# Revit family: FS_Reynaers_SL38 Cubic_Window Fixed
name_source: partatom
category: Окна
revit_build: Autodesk Revit 2017 (Build: 20160225_1515(x64)
units: mm (PartAtom-declared; Revit-internal decimal feet)

## family parameters
Всегда вертикально = Да
Заголовок OmniClass = Windows
Номер OmniClass = 23.30.20.00
Общий = Нет
Основа = Стена
При загрузке вырезать с полостями = Нет
Точка расчета площади = Нет

## types (1)
- Frame 38.5
    BE = Да
    Date of publishing = 2015-11-19
    Default Sill Height = 800 мм
    Design country = Belgium
    Edition number = 1
    IFC Classification = Window
    Manufacturer country = Belgium
    Manufacturer name = Reynaers
    Material main = Aluminium
    Material secondary = Aluminium
    NBS Reference Code = 59-97
    NBS Reference Description = Windows
    NL = Нет
    Nominal height = 0
    Nominal width = 0
    Product Guid = e351ed82-0458-4031-8220-8276baccd360
    Product SKU = Reynaers_window_Slim_Line_38
    Product data url = http://file-system.ru
    Product family = Windows & Doors
    Product group = Windows Aluminium
    REY Built-In Depth = 86 мм
    REY Butt Strip Width = 10 мм
    REY Design = 0 мм
    REY Fixation Bottom = 38 мм
    REY Frame Width = 39 мм
    REY Gap Width = 0 мм
    REY Joint Bottom = 5 мм
    REY Joint Width = 5 мм
    REY Joint Width A = 0 мм
    REY Joint Width B = 5 мм
    REY Offset Wall Ext Int = 50 мм
    REY Offset Wall Ext Int A = 0 мм
    REY Offset Wall Ext Int B = 50 мм
    REY Panel Coverage = 10 мм
    REY Profile Rebate = 25 мм
    REY Rebate = 20 мм
    REY Rebate A = 0 мм
    REY Rebate B = 20 мм
    REY Rebate TOP A = 0 мм
    REY Rebate TOP B = 20 мм
    REY Shutter = Нет
    REY Shutter Depth = 0 мм
    REY Shutter Height = 0 мм
    REY Shutter Position = 0 мм
    REY Shutter Roll Height = 200 мм
    REY Shutter Roll Material = <По категории>
    REY Sill = Нет
    REY Sill H = 0 мм
    REY Sill Height = 35 мм
    REY Vent & Gap = 0 мм
    REY Vent Width = 0 мм
    REY Website = www.reynaers.com
    UNSPSC Code = 301716
    URL = http://www.reynaers.com
    Uniclass 1.4 Code = JL10
    Uniclass 1.4 Description = Windows
    Uniclass 2.0 Code = PR-59-97
    Uniclass 2.0 Description = Windows
    Wall Exterior Width = 90 мм
    Weight Net (Kg) = 0
    Аналитическая конструкция = <None>
    Замыкание стены = По основе
    Изготовитель = Reynaers

## geometry (parser evidence)
native form markers: Blend x4, Sweep x4
no freeform markers — native parametric forms only
